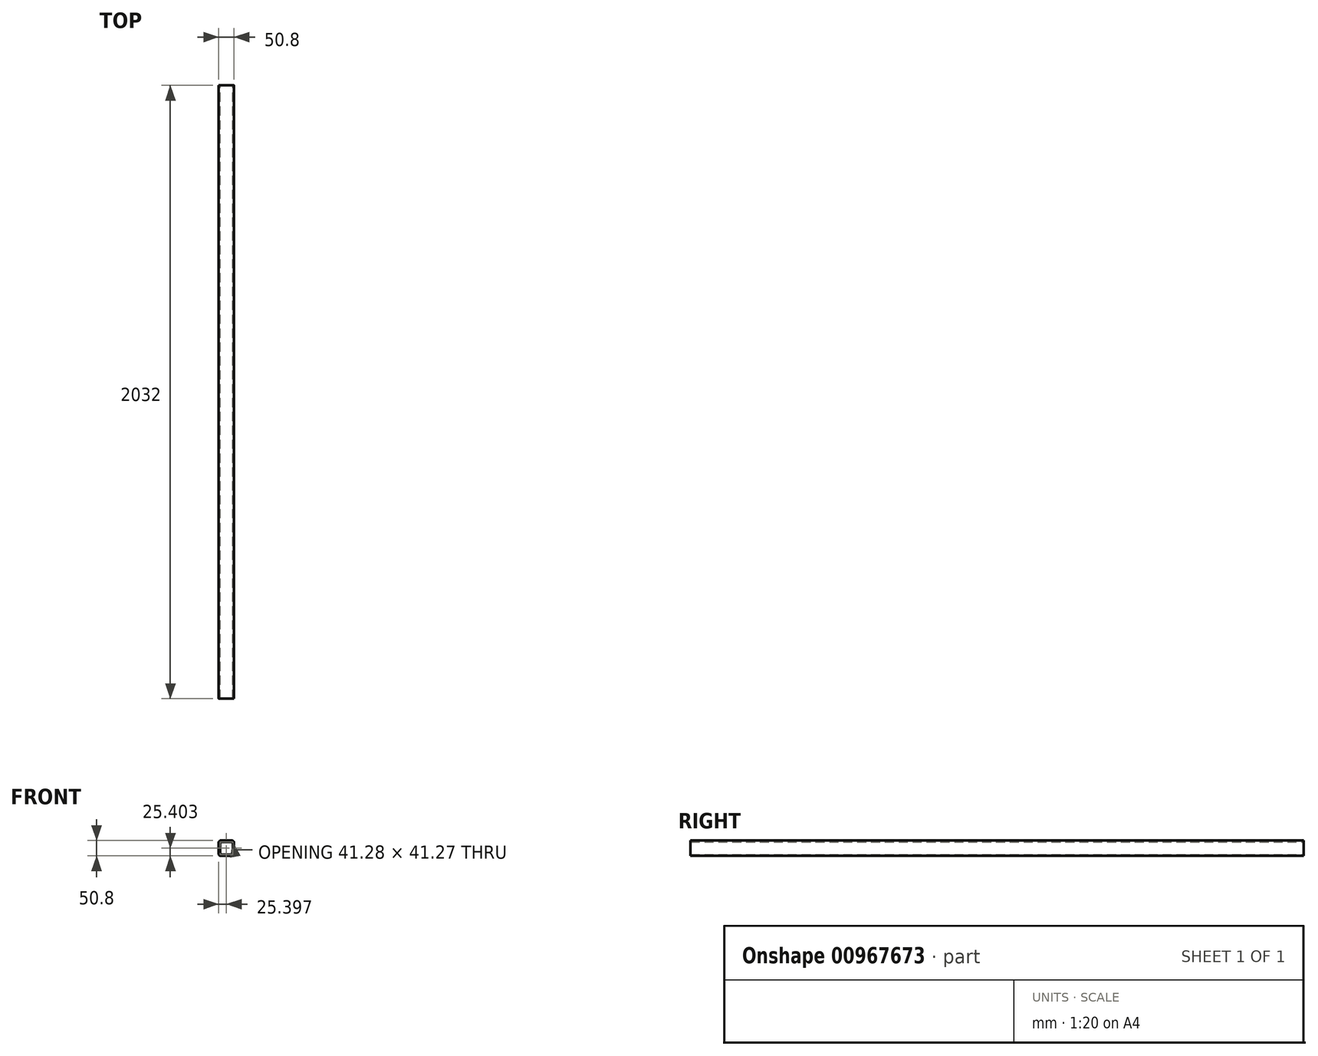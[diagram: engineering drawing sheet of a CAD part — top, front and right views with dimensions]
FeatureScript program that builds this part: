
annotation { "Feature Type Name" : "Feature", "Feature Type Description" : "" }
export const myFeature = defineFeature(function(context is Context, id is Id, definition is map)
    precondition{}
    {
        {
            var Q0;
            Q0=qCreatedBy(makeId("Front.planeOp"),FACE);
            var sketch = newSketch(context, id + "F0", { "sketchPlane" : qUnion([Q0])});
            skLineSegment(sketch, "E0.bottom", {"start": v(-122.65, 54.21) * mm, "end": v(-84.55, 54.21) * mm});
            skLineSegment(sketch, "E0.top", {"start": v(-122.65, 105.01) * mm, "end": v(-84.55, 105.01) * mm});
            skLineSegment(sketch, "E0.left", {"start": v(-129, 60.56) * mm, "end": v(-129, 98.66) * mm});
            skLineSegment(sketch, "E0.right", {"start": v(-78.2, 60.56) * mm, "end": v(-78.2, 98.66) * mm});
            skPoint(sketch, "E1.visualSharp", {"position": v(-129, 105.01) * mm});
            skArc(sketch, "E1.filletArc", {"start": v(-122.65, 105.01) * mm, "mid": v(-127.14, 103.15) * mm, "end": v(-129, 98.66) * mm});
            skPoint(sketch, "E2.visualSharp", {"position": v(-78.2, 105.01) * mm});
            skArc(sketch, "E2.filletArc", {"start": v(-78.2, 98.66) * mm, "mid": v(-80.06, 103.15) * mm, "end": v(-84.55, 105.01) * mm});
            skPoint(sketch, "E3.visualSharp", {"position": v(-78.2, 54.21) * mm});
            skArc(sketch, "E3.filletArc", {"start": v(-84.55, 54.21) * mm, "mid": v(-80.06, 56.07) * mm, "end": v(-78.2, 60.56) * mm});
            skPoint(sketch, "E4.visualSharp", {"position": v(-129, 54.21) * mm});
            skArc(sketch, "E4.filletArc", {"start": v(-129, 60.56) * mm, "mid": v(-127.14, 56.07) * mm, "end": v(-122.65, 54.21) * mm});
            skArc(sketch, "E5.0", {"start": v(-122.65, 100.25) * mm, "mid": v(-123.78, 99.79) * mm, "end": v(-124.24, 98.66) * mm});
            skLineSegment(sketch, "E5.1", {"start": v(-124.24, 60.56) * mm, "end": v(-124.24, 98.66) * mm});
            skLineSegment(sketch, "E5.2", {"start": v(-122.65, 100.25) * mm, "end": v(-84.55, 100.25) * mm});
            skArc(sketch, "E5.3", {"start": v(-124.24, 60.56) * mm, "mid": v(-123.78, 59.44) * mm, "end": v(-122.65, 58.98) * mm});
            skArc(sketch, "E5.4", {"start": v(-82.97, 98.66) * mm, "mid": v(-83.43, 99.79) * mm, "end": v(-84.55, 100.25) * mm});
            skLineSegment(sketch, "E5.5", {"start": v(-82.97, 60.56) * mm, "end": v(-82.97, 98.66) * mm});
            skArc(sketch, "E5.6", {"start": v(-84.55, 58.98) * mm, "mid": v(-83.43, 59.44) * mm, "end": v(-82.97, 60.56) * mm});
            skLineSegment(sketch, "E5.7", {"start": v(-122.65, 58.98) * mm, "end": v(-84.55, 58.98) * mm});
            skSolve(sketch);
        }
        {
            var Q0;
            Q0 = qSketchRegion(id + "F0", true);
            extrude(context, id + "F1", {"entities" : qUnion([Q0]), "depth" : 2032 * mm, "offsetDistance" : 25.4 * mm});
        }
    });
